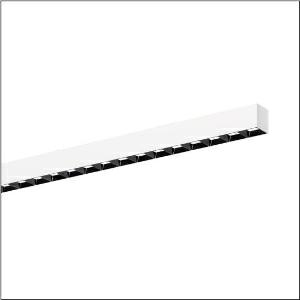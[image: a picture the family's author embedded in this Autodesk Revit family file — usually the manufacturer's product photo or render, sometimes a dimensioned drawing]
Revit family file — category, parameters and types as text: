
# Revit family: silica_r__21_51mx22dc3awb_a852
name_source: partatom
category: Lighting Fixtures
units: mm (PartAtom-declared; Revit-internal decimal feet)

## family parameters
Cut with Voids When Loaded = No
Host = Face
Light Source = No
Part Type = Normal
Room Calculation Point = No
Round Connector Dimension = Use Diameter
Shared = No

## types (1)
- --- (1 x LED, 10800 lm, 69.2 W, 3000K)
    Apparent Load = 69 VA
    CIE Flux Codes = 86 100 100 100 100
    Color Rendering = 80
    Color Temperature = 3000K
    Default Elevation = 1800 mm
    Description = Silica® 21, office luminaire, primary light control with darklight reflector, of PMMA, black, CAT 2 (L<= 3000cd/m²), light emission: direct distribution, primary light characteristic: symmetric, installation type: surface-mounted, LED, rated luminous flux: 10.800lm, luminous efficacy: 156lm/W, light colour: 830, colour temperature: 3000K, with terminal, 3+2-pole, max. 2.5mm², mains connection: 220..240V, AC, 50/60Hz, rated input power: 69.2W, luminaire housing, of aluminium, traffic white (RAL 9016), length: 3.004mm, width: 53mm, height: 53mm, protection rating (complete): IP20, insulation class (complete): insulation class I (protective earthing), certification: CE, permissible operating ambient temperature: 0..+35°C, standard: EN 50419, packaging unit: 1 piece
    Height = 0 mm  [stored 0 ft]
    Lamp = 1 x LED
    Lamp Light Flux = 10800 lm
    Lamp Power = 69.2 W
    Lamp count = 1
    Length = 3004 mm
    Luminous efficacy = 156 lm/W
    Manufacturer = Siteco
    ModVariant = No
    Model = 51MX22DC3AWB
    Mounting Place = Ceiling
    Mounting Type = Recessed
    Number of Poles = 1
    OnlyDefault = Yes
    Power Factor = 1
    Product Name = Silica® 21
    Product group = office luminaire | ceiling recessed
    ProductGroupID = 401
    Protection Class = Protection class I
    Protection Degree = IP 20
    RLX_Detail_Level = 1
    RLX_Emergency_Light_Flux = 0 lm
    RLX_Emergency_Type = 0
    RLX_Emergency_Type_DB = No
    RlxData = <blob elided: 62153 chars, md5=9d54b121>
    Socket = socket
    Standby Power = 0 W
    System Light Flux = 10800 lm
    System Power = 69 W
    Type Comments = factory setting: luminous flux: 100 % | dim-lin: 254 | 392 mA
    Type Image = l_1313592.jpg
    URL = http://relux.com
    VarID = @adj_074449
    Voltage = 0 V
    Weight = 0.00 kg
    Width = 53 mm

note: [stored X ft] marks values corroborated as IEEE doubles in the binary element streams (Revit-internal decimal feet)

## geometry (parser evidence)
native form markers: Blend x4, Sweep x10
no freeform markers — native parametric forms only
